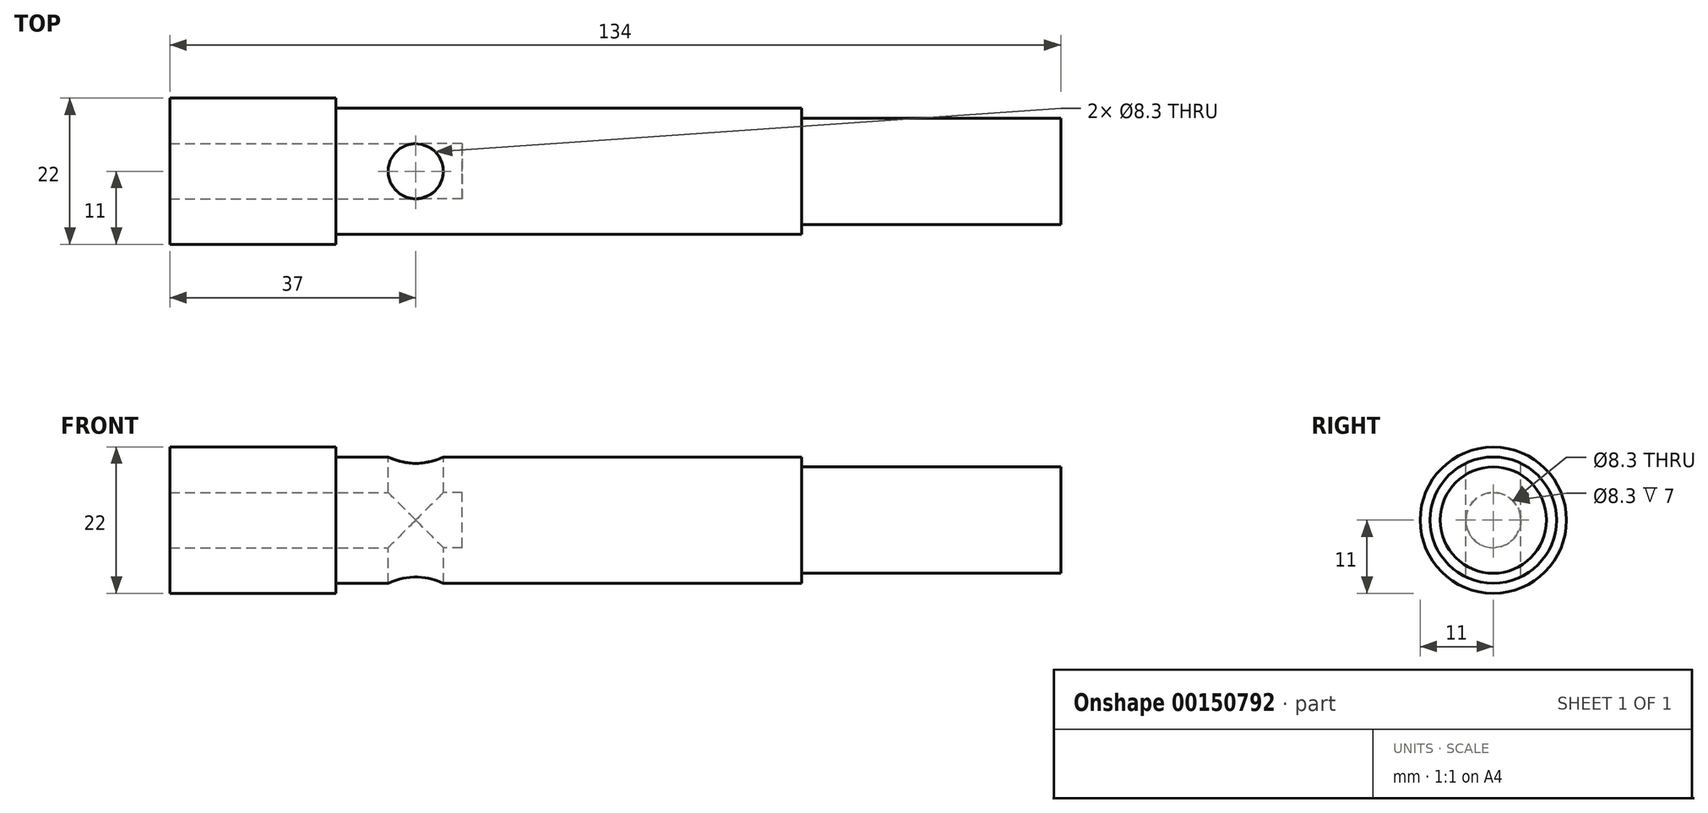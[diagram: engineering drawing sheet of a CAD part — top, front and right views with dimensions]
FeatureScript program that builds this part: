
annotation { "Feature Type Name" : "Feature", "Feature Type Description" : "" }
export const myFeature = defineFeature(function(context is Context, id is Id, definition is map)
    precondition{}
    {
        {
            var Q0;
            Q0=qCreatedBy(makeId("Right.planeOp"),FACE);
            var sketch = newSketch(context, id + "F0", { "sketchPlane" : qUnion([Q0])});
            skCircle(sketch, "E0", {"center": v(0, 0) * mm, "radius": 4.15 * mm});
            skCircle(sketch, "E1", {"center": v(0, 0) * mm, "radius": 11 * mm});
            skSolve(sketch);
        }
        {
            var Q0;
            Q0=qSketchRegion(id+"F0",true);
            extrude(context, id + "F1", {"entities" : qUnion([Q0]), "oppositeDirection" : true, "depth" : 25 * mm});
        }
        {
            var Q0;
            Q0=makeQuery(id+"F1.opExtrude","CAP_FACE",FACE,{"disambiguationData":[OSD([sQuery(id+"F0.wireOp",EDGE,"E0"),sQuery(id+"F0.wireOp",EDGE,"E1")])],"isStart":true});
            var sketch = newSketch(context, id + "F2", { "sketchPlane" : qUnion([Q0])});
            skCircle(sketch, "E2", {"center": v(0, 0) * mm, "radius": 9.5 * mm});
            skSolve(sketch);
        }
        {
            var Q0;
            Q0=qSketchRegion(id+"F2",true);
            extrude(context, id + "F3", {"entities" : qUnion([Q0]), "operationType" : NewBodyOperationType.ADD, "depth" : 70 * mm});
        }
        {
            var Q0;
            Q0=qCreatedBy(makeId("Origin.pointOp"),VERTEX);
            var Q1;
            Q1=qCreatedBy(makeId("Top.planeOp"),FACE);
            cPlane(context, id + "F4", {"entities" : qUnion([Q0, Q1]), "cplaneType" : CPlaneType.PLANE_POINT, "offset" : 25 * mm, "width" : 150 * mm, "height" : 150 * mm});
        }
        {
            var Q0;
            Q0=qCreatedBy(id+"F4.planeOp",FACE);
            var sketch = newSketch(context, id + "F5", { "sketchPlane" : qUnion([Q0])});
            skCircle(sketch, "E3", {"center": v(12, 0) * mm, "radius": 4.15 * mm});
            skSolve(sketch);
        }
        {
            var Q0;
            Q0=qSketchRegion(id+"F5",true);
            extrude(context, id + "F6", {"entities" : qUnion([Q0]), "operationType" : NewBodyOperationType.REMOVE, "endBound" : BoundingType.THROUGH_ALL, "oppositeDirection" : true, "depth" : 25 * mm, "hasSecondDirection" : true, "secondDirectionBound" : SecondDirectionBoundingType.THROUGH_ALL, "secondDirectionOppositeDirection" : false, "secondDirectionDepth" : 25 * mm});
        }
        {
            var Q0;
            Q0=makeQuery(id+"F3.opExtrude","CAP_FACE",FACE,{"disambiguationData":[OSD([sQuery(id+"F2.wireOp",EDGE,"E2")])],"isStart":false});
            var sketch = newSketch(context, id + "F7", { "sketchPlane" : qUnion([Q0])});
            skCircle(sketch, "E4", {"center": v(0, 0) * mm, "radius": 8 * mm});
            skSolve(sketch);
        }
        {
            var Q0;
            Q0=qSketchRegion(id+"F7",true);
            extrude(context, id + "F8", {"entities" : qUnion([Q0]), "operationType" : NewBodyOperationType.ADD, "depth" : 39 * mm});
        }
        {
            var Q0;
            Q0=makeQuery(id+"F3.opExtrude","CAP_FACE",FACE,{"disambiguationData":[OSD([sQuery(id+"F2.wireOp",EDGE,"E2")])],"isStart":true});
            extrude(context, id + "F9", {"entities" : qUnion([Q0]), "operationType" : NewBodyOperationType.REMOVE, "oppositeDirection" : true, "depth" : 19 * mm});
        }
    });
